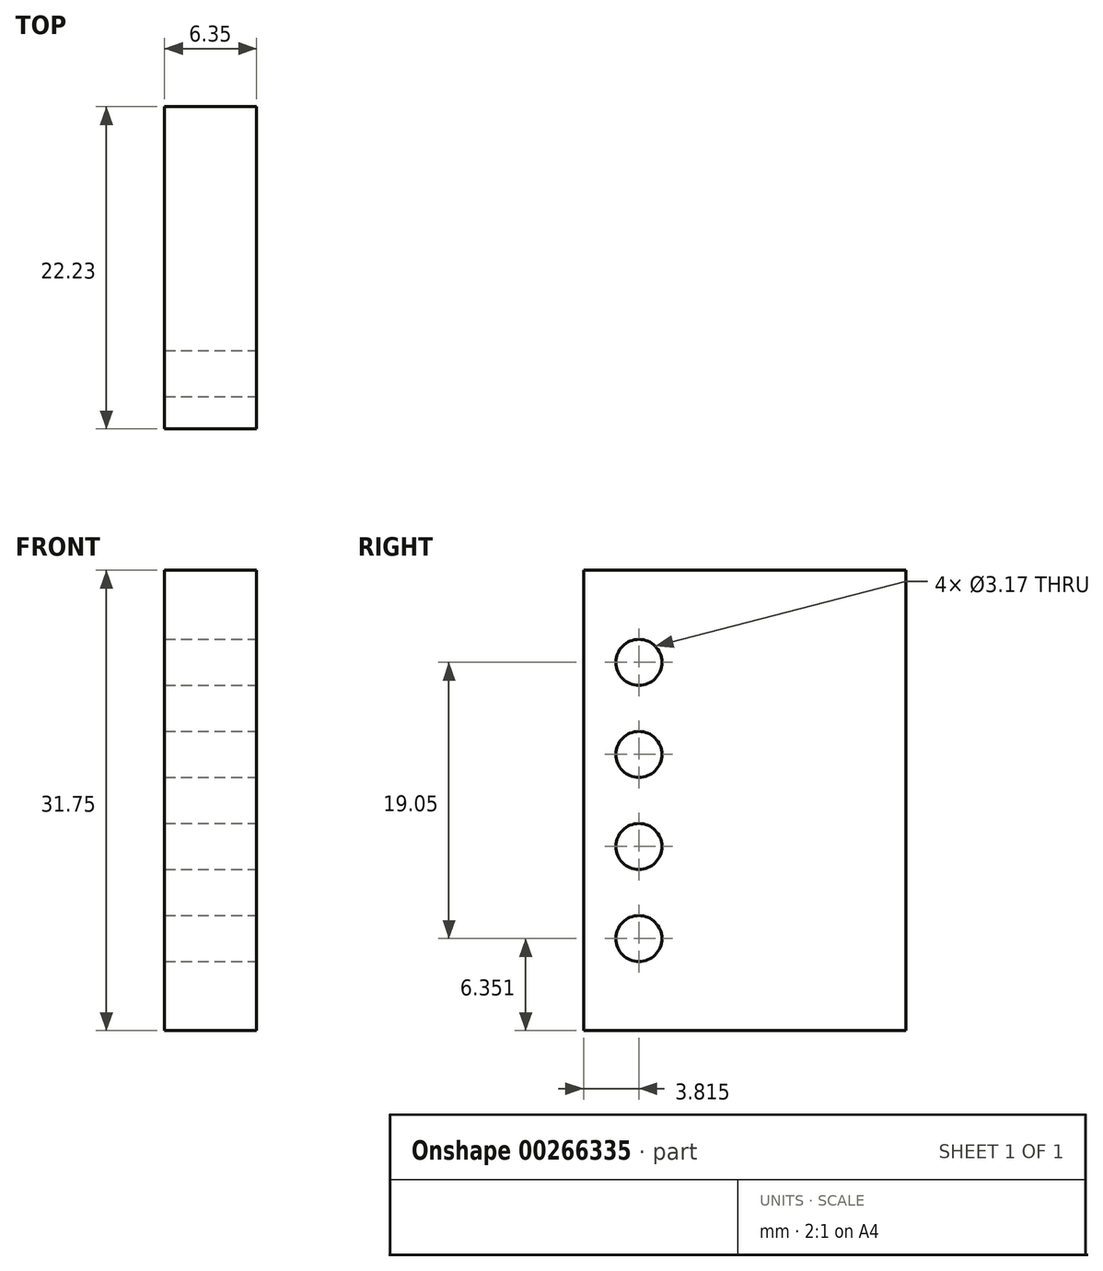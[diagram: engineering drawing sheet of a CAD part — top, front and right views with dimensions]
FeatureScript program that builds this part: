
annotation { "Feature Type Name" : "Feature", "Feature Type Description" : "" }
export const myFeature = defineFeature(function(context is Context, id is Id, definition is map)
    precondition{}
    {
        {
            var Q0;
            Q0=qCreatedBy(makeId("Front.planeOp"),FACE);
            var sketch = newSketch(context, id + "F0", { "sketchPlane" : qUnion([Q0])});
            skLineSegment(sketch, "E0.bottom", {"start": v(-6.35, 2.96) * mm, "end": v(0, 2.96) * mm});
            skLineSegment(sketch, "E0.top", {"start": v(-6.35, 34.71) * mm, "end": v(0, 34.71) * mm});
            skLineSegment(sketch, "E0.left", {"start": v(-6.35, 2.96) * mm, "end": v(-6.35, 34.71) * mm});
            skLineSegment(sketch, "E0.right", {"start": v(0, 2.96) * mm, "end": v(0, 34.71) * mm});
            skSolve(sketch);
        }
        {
            var Q0;
            Q0=makeQuery(id+"F0.imprint","IMPRINT",FACE,{"disambiguationData":[TD([[makeQuery(id+"F0.imprint","IMPRINT",EDGE,{"derivedFrom":sQuery(id+"F0.wireOp",EDGE,"E0.bottom")}),1.0]])]});
            extrude(context, id + "F1", {"entities" : qUnion([Q0]), "depth" : 22.22 * mm, "offsetDistance" : 25.4 * mm});
        }
        {
            var Q0;
            Q0=makeQuery(id+"F1.opExtrude","SWEPT_FACE",FACE,{"disambiguationData":[OSD([sQuery(id+"F0.wireOp",EDGE,"E0.right")])]});
            var sketch = newSketch(context, id + "F2", { "sketchPlane" : qUnion([Q0])});
            skCircle(sketch, "E1", {"center": v(-18.41, 28.36) * mm, "radius": 1.59 * mm});
            skCircle(sketch, "E2", {"center": v(-18.41, 22.01) * mm, "radius": 1.59 * mm});
            skCircle(sketch, "E3", {"center": v(-18.41, 9.31) * mm, "radius": 1.59 * mm});
            skCircle(sketch, "E4", {"center": v(-18.41, 15.66) * mm, "radius": 1.59 * mm});
            skSolve(sketch);
        }
        {
            var Q0;
            Q0=makeQuery(id+"F2.imprint","IMPRINT",FACE,{"disambiguationData":[TD([[makeQuery(id+"F2.imprint","IMPRINT",EDGE,{"derivedFrom":sQuery(id+"F2.wireOp",EDGE,"E2")}),1.0]])]});
            var Q1;
            Q1=makeQuery(id+"F2.imprint","IMPRINT",FACE,{"disambiguationData":[TD([[makeQuery(id+"F2.imprint","IMPRINT",EDGE,{"derivedFrom":sQuery(id+"F2.wireOp",EDGE,"E4")}),1.0]])]});
            var Q2;
            Q2=makeQuery(id+"F2.imprint","IMPRINT",FACE,{"disambiguationData":[TD([[makeQuery(id+"F2.imprint","IMPRINT",EDGE,{"derivedFrom":sQuery(id+"F2.wireOp",EDGE,"E3")}),1.0]])]});
            var Q3;
            Q3=makeQuery(id+"F2.imprint","IMPRINT",FACE,{"disambiguationData":[TD([[makeQuery(id+"F2.imprint","IMPRINT",EDGE,{"derivedFrom":sQuery(id+"F2.wireOp",EDGE,"E1")}),1.0]])]});
            extrude(context, id + "F3", {"entities" : qUnion([Q0, Q1, Q2, Q3]), "operationType" : NewBodyOperationType.REMOVE, "oppositeDirection" : true, "depth" : 6.35 * mm, "offsetDistance" : 25.4 * mm});
        }
    });
